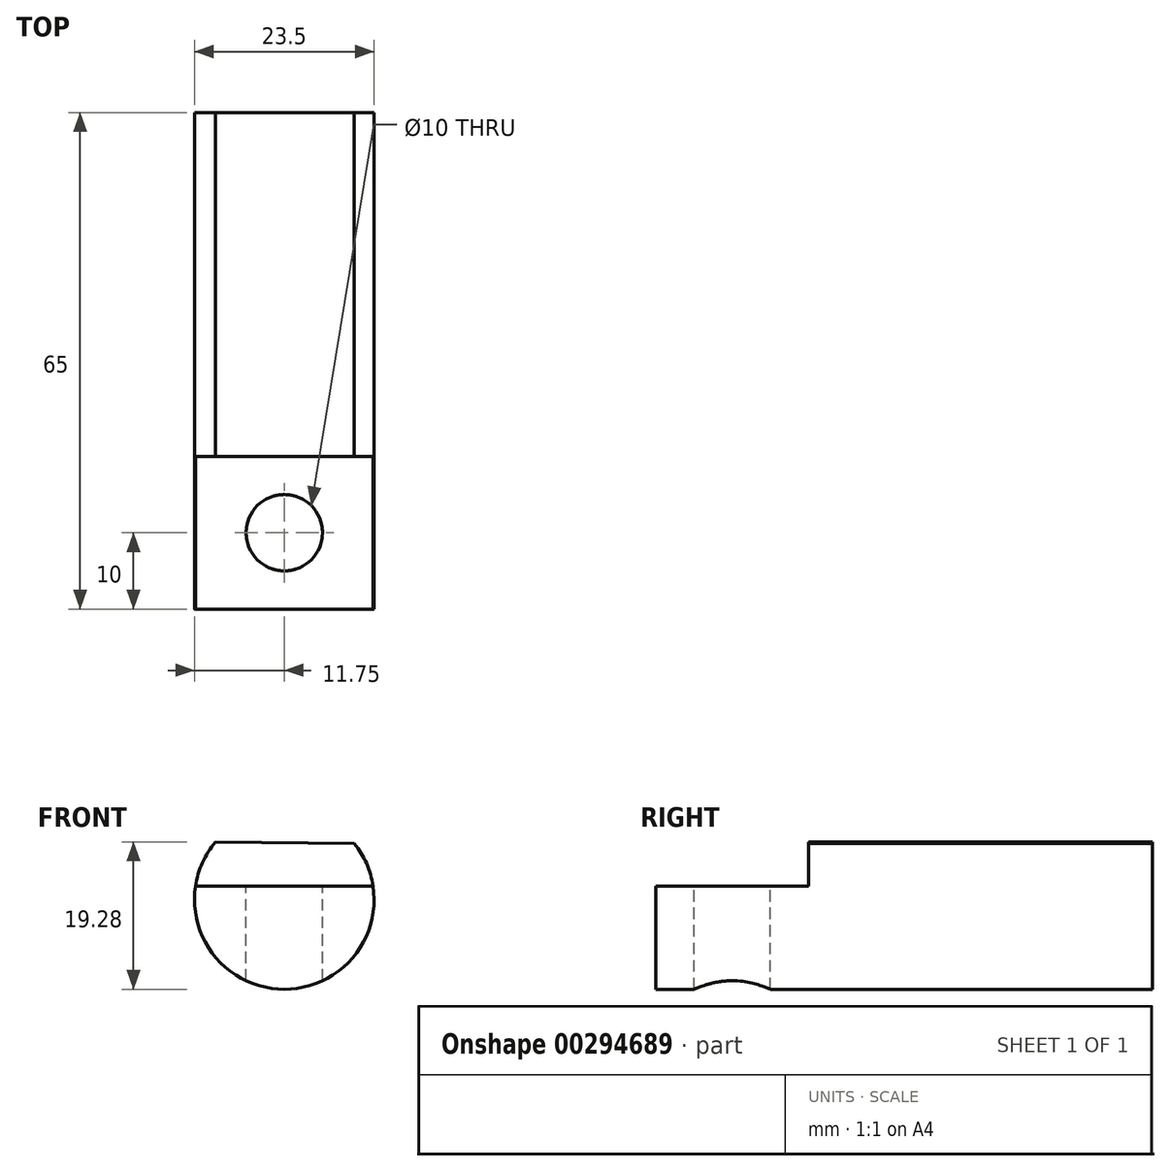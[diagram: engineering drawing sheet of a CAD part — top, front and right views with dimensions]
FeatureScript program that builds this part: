
annotation { "Feature Type Name" : "Feature", "Feature Type Description" : "" }
export const myFeature = defineFeature(function(context is Context, id is Id, definition is map)
    precondition{}
    {
        {
            var Q0;
            Q0=qCreatedBy(makeId("Front.planeOp"),FACE);
            var sketch = newSketch(context, id + "F0", { "sketchPlane" : qUnion([Q0])});
            skCircle(sketch, "E0", {"center": v(0, 0) * mm, "radius": 11.75 * mm});
            skSolve(sketch);
        }
        {
            var Q0;
            Q0 = qSketchRegion(id + "F0", true);
            extrude(context, id + "F1", {"entities" : qUnion([Q0]), "depth" : 65 * mm});
        }
        {
            var Q0;
            Q0=makeQuery(id+"F1.opExtrude","CAP_FACE",FACE,{"disambiguationData":[OSD([sQuery(id+"F0.wireOp",EDGE,"E0")])],"isStart":false});
            var sketch = newSketch(context, id + "F2", { "sketchPlane" : qUnion([Q0])});
            skLineSegment(sketch, "E1", {"start": v(-11.62, 1.75) * mm, "end": v(11.62, 1.75) * mm});
            skArc(sketch, "E2", {"start": v(11.62, 1.75) * mm, "mid": v(0, 11.75) * mm, "end": v(-11.62, 1.75) * mm});
            skSolve(sketch);
        }
        {
            var Q0;
            Q0 = qSketchRegion(id + "F2", true);
            extrude(context, id + "F3", {"entities" : qUnion([Q0]), "operationType" : NewBodyOperationType.REMOVE, "oppositeDirection" : true, "depth" : 20 * mm});
        }
        {
            var Q0;
            Q0=makeQuery(id+"F3.boolean.opBoolean","COPY",FACE,{"derivedFrom":makeQuery(id+"F3.opExtrude","SWEPT_FACE",FACE,{"disambiguationData":[OSD([sQuery(id+"F2.wireOp",EDGE,"E1")])]})});
            var sketch = newSketch(context, id + "F4", { "sketchPlane" : qUnion([Q0])});
            skCircle(sketch, "E3", {"center": v(0, -55) * mm, "radius": 5 * mm});
            skPoint(sketch, "E3.centerSnap0", {"position": v(11.62, -55) * mm});
            skPoint(sketch, "E3.centerSnap1", {"position": v(0, -45) * mm});
            skSolve(sketch);
        }
        {
            var Q0;
            Q0 = qSketchRegion(id + "F4", true);
            extrude(context, id + "F5", {"entities" : qUnion([Q0]), "operationType" : NewBodyOperationType.REMOVE, "endBound" : BoundingType.THROUGH_ALL, "oppositeDirection" : true, "depth" : 25 * mm});
        }
        {
            var Q0;
            Q0=makeQuery(id+"F3.boolean.opBoolean","COPY",FACE,{"derivedFrom":makeQuery(id+"F3.opExtrude","CAP_FACE",FACE,{"disambiguationData":[OSD([sQuery(id+"F2.wireOp",EDGE,"E1"),sQuery(id+"F2.wireOp",EDGE,"E2")])],"isStart":false})});
            var sketch = newSketch(context, id + "F6", { "sketchPlane" : qUnion([Q0])});
            skLineSegment(sketch, "E4", {"start": v(-9.02, 7.53) * mm, "end": v(9.02, 7.53) * mm, "construction": true});
            skArc(sketch, "E5", {"start": v(9.17, 7.34) * mm, "mid": v(0.12, 11.75) * mm, "end": v(-9.02, 7.53) * mm});
            skLineSegment(sketch, "E6", {"start": v(-9.02, 7.53) * mm, "end": v(9.17, 7.34) * mm});
            skArc(sketch, "E7", {"start": v(-9.02, 7.53) * mm, "mid": v(0, -11.75) * mm, "end": v(9.02, 7.53) * mm, "construction": true});
            skSolve(sketch);
        }
        {
            var Q0;
            Q0=makeQuery(id+"F6.imprint","IMPRINT",FACE,{"disambiguationData":[TD([[makeQuery(id+"F6.imprint","IMPRINT",EDGE,{"derivedFrom":sQuery(id+"F6.wireOp",EDGE,"E5")}),1.0]])]});
            extrude(context, id + "F7", {"entities" : qUnion([Q0]), "operationType" : NewBodyOperationType.REMOVE, "endBound" : BoundingType.THROUGH_ALL, "oppositeDirection" : true, "depth" : 25 * mm});
        }
    });
